# Revit family: e15e426f-0c8b-4ec2-bcfa-d793507aa1c2
name_source: partatom
category: Plumbing Fixtures
revit_build: Autodesk Revit 2014 (Build: 20130308_1515(x64)
units: mm (PartAtom-declared; Revit-internal decimal feet)

## types (1)
- e15e426f-0c8b-4ec2-bcfa-d793507aa1c2
    Assembly Code = D2010510
    Capacity = as Specified
    Default Elevation = 0' - 0"
    Expected Lifespan (Years) = 0
    Fixture Finish = Finish - TOTO - Cotton 01
    Keynote = 22 40 00
    Maintenance Schedule (Months) = 0
    Manufacturer = TOTO USA
    Manufacturer Fax = 770-282-8697
    Manufacturer Website = http://www.totousa.com
    Model = As Specified
    Product Data = http://www.arcat.com
    Revision = R1_2016-12
    Sales Information = http://www.totousa.com
    Standards Conformance = as Specified
    URL = http://www.totousa.com
    Unit Depth = 4' - 7 1/8"
    Unit Height = 0' - 3 1/8"
    Unit Weight = 883
    Unit Width = 5' - 10 7/8"
    Warranty Duration (Years) = 0

## geometry (parser evidence)
native form markers: Sweep x6
no freeform markers — native parametric forms only
